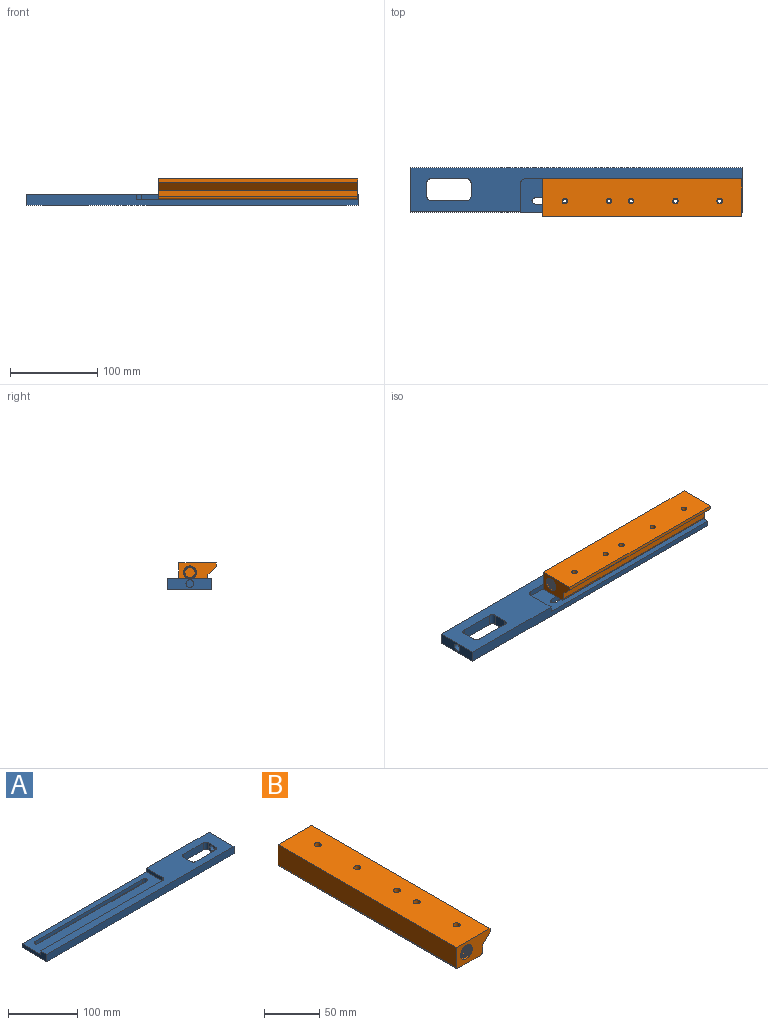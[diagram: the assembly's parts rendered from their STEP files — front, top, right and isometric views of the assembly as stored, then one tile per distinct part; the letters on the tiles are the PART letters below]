
ASSEMBLY  parts=2 mates=1
PART A: 25 faces, bbox 381x50.8x12.7 mm
  f0: plane 381x50.8mm, normal (0,0,-1), area 16366.6mm2, adj f2,f3,f5,f6,f9,f10,f11,f12
  f1: plane 254x38.1mm, normal (0,0,1), area 7951.8mm2, adj f2,f3,f7,f8,f13,f14,f15,f16
  f2: plane 50.8x12.7mm, normal (-1,0,0), area 403.2mm2, adj f0,f1,f3,f4,f5,f8
  f3: plane 381x12.7mm, normal (0,1,0), area 3225.8mm2, adj f0,f1,f2,f4,f6,f7
  f4: plane 381x50.8mm, normal (0,0,1), area 8414.8mm2, adj f2,f3,f5,f6,f7,f8,f9,f10
  f5: plane 381x12.7mm, normal (0,-1,0), area 4838.7mm2, adj f0,f2,f4,f6
  f6: plane 50.8x12.7mm, normal (1,0,0), area 583.1mm2, adj f0,f3,f4,f5,f24
  f7: plane 33.02x6.35mm, normal (-1,0,0), area 209.7mm2, adj f1,f3,f4,f23
  f8: plane 248.92x6.35mm, normal (0,1,0), area 1580.6mm2, adj f1,f2,f4,f23
  f9: plane 15.24x12.7mm, normal (1,0,0), area 193.5mm2, adj f0,f4,f19,f22
  f10: plane 40.64x12.7mm, normal (0,1,0), area 516.1mm2, adj f0,f4,f19,f20
  f11: plane 15.24x12.7mm, normal (-1,0,0), area 131.5mm2, adj f0,f4,f20,f21,f24
  f12: plane 40.64x12.7mm, normal (0,-1,0), area 516.1mm2, adj f0,f4,f21,f22
  f13: plane 218.44x6.35mm, normal (0,-1,0), area 1387.1mm2, adj f0,f1,f16,f17
  f14: plane 218.44x6.35mm, normal (0,1,0), area 1387.1mm2, adj f0,f1,f15,f18
  f15: cylinder r=5.08mm len=6.35mm, axis (0,0,-1), area 42.5mm2, adj f0,f1,f14,f16
  f16: cylinder r=5.08mm len=6.35mm, axis (0,0,1), area 42.5mm2, adj f0,f1,f13,f15
  f17: cylinder r=5.08mm len=6.35mm, axis (0,0,-1), area 42.5mm2, adj f0,f1,f13,f18
  f18: cylinder r=5.08mm len=6.35mm, axis (0,0,1), area 42.5mm2, adj f0,f1,f14,f17
  f19: cylinder r=5.08mm len=12.7mm, axis (0,0,-1), area 101.3mm2, adj f0,f4,f9,f10
  f20: cylinder r=5.08mm len=12.7mm, axis (0,0,1), area 101.3mm2, adj f0,f4,f10,f11
  f21: cylinder r=5.08mm len=12.7mm, axis (0,0,-1), area 101.3mm2, adj f0,f4,f11,f12
  f22: cylinder r=5.08mm len=12.7mm, axis (0,0,1), area 101.3mm2, adj f0,f4,f9,f12
  f23: cylinder r=5.08mm len=6.35mm, axis (0,0,1), area 50.7mm2, adj f1,f4,f7,f8
  f24: cylinder r=4.45mm len=19.24mm, axis (1,0,0), area 537.4mm2, adj f6,f11
PART B: 129 faces, bbox 42.9x228.9x23.9 mm
  f0: cylinder r=3.17mm len=13.02mm, axis (0,0,1), area 235.9mm2, adj f1,f87,f125,f126,f128
  f1: cylinder r=3.17mm len=6.35mm, axis (0,0,1), area 3.2mm2, adj f0,f2,f126,f128
  f2: cylinder r=3.17mm len=6.35mm, axis (0,0,1), area 3.2mm2, adj f1,f3,f126,f128
  f3: cylinder r=3.17mm len=6.35mm, axis (0,0,1), area 3.2mm2, adj f2,f4,f126,f128
  f4: cylinder r=3.17mm len=6.35mm, axis (0,0,1), area 3.2mm2, adj f3,f5,f126,f128
  f5: cylinder r=3.17mm len=6.35mm, axis (0,0,1), area 3.2mm2, adj f4,f6,f126,f128
  f6: cylinder r=3.17mm len=6.35mm, axis (0,0,1), area 3.2mm2, adj f5,f7,f126,f128
  f7: cylinder r=3.17mm len=6.35mm, axis (0,0,1), area 3.2mm2, adj f6,f8,f126,f128
  f8: cylinder r=3.17mm len=6.35mm, axis (0,0,1), area 3.2mm2, adj f7,f9,f126,f128
  f9: cylinder r=3.17mm len=6.01mm, axis (0,0,1), area 1.1mm2, adj f8,f10,f126,f128
  f10: cone r=3.43mm half-angle=45deg, axis (0,0,-1), area 18mm2, adj f9,f80,f126,f127,f128
  f11: cone r=3.43mm half-angle=45deg, axis (0,0,-1), area 18mm2, adj f21,f80,f122,f123,f124
  f12: cylinder r=3.17mm len=13.02mm, axis (0,0,1), area 235.9mm2, adj f13,f87,f121,f122,f124
  f13: cylinder r=3.17mm len=6.35mm, axis (0,0,1), area 3.2mm2, adj f12,f14,f122,f124
  f14: cylinder r=3.17mm len=6.35mm, axis (0,0,1), area 3.2mm2, adj f13,f15,f122,f124
  f15: cylinder r=3.17mm len=6.35mm, axis (0,0,1), area 3.2mm2, adj f14,f16,f122,f124
  f16: cylinder r=3.17mm len=6.35mm, axis (0,0,1), area 3.2mm2, adj f15,f17,f122,f124
  f17: cylinder r=3.17mm len=6.35mm, axis (0,0,1), area 3.2mm2, adj f16,f18,f122,f124
  f18: cylinder r=3.17mm len=6.35mm, axis (0,0,1), area 3.2mm2, adj f17,f19,f122,f124
  f19: cylinder r=3.17mm len=6.35mm, axis (0,0,1), area 3.2mm2, adj f18,f20,f122,f124
  f20: cylinder r=3.17mm len=6.35mm, axis (0,0,1), area 3.2mm2, adj f19,f21,f122,f124
  f21: cylinder r=3.17mm len=6.01mm, axis (0,0,1), area 1.1mm2, adj f11,f20,f122,f124
  f22: cone r=3.43mm half-angle=45deg, axis (0,0,-1), area 17.9mm2, adj f70,f71,f72,f73,f80
  f23: cone r=3.43mm half-angle=45deg, axis (0,0,-1), area 17.9mm2, adj f60,f74,f75,f76,f80
  f24: cone r=3.43mm half-angle=45deg, axis (0,0,-1), area 17.9mm2, adj f50,f77,f78,f79,f80
  f25: cone r=7.18mm half-angle=1.8deg, axis (0,0,-1), area 68mm2, adj f27,f28,f114,f116,f117
  f26: cylinder r=6.86mm len=13.72mm, axis (0,0,-1), area 220.4mm2, adj f27,f111,f112,f113,f116
  f27: cylinder r=6.86mm len=13.72mm, axis (0,0,-1), area 6.7mm2, adj f25,f26,f114,f116
  f28: cone r=7.56mm half-angle=45deg, axis (0,0,-1), area 51.4mm2, adj f25,f80,f115,f116,f117
  f29: cone r=6.86mm half-angle=1.8deg, axis (0,1,0), area 60.7mm2, adj f30,f31,f108,f110
  f30: cylinder r=6.86mm len=13.72mm, axis (0,1,0), area 226.7mm2, adj f29,f104,f105,f106,f107,f110
  f31: cone r=7.56mm half-angle=45deg, axis (0,1,0), area 52.8mm2, adj f29,f32,f81,f108,f109,f110
  f32: cone r=7.56mm half-angle=45deg, axis (0,1,0), area 0.6mm2, adj f31,f108,f109
  f33: cone r=7.18mm half-angle=1.8deg, axis (0,0,-1), area 68mm2, adj f35,f36,f100,f102,f103
  f34: cylinder r=6.86mm len=13.72mm, axis (0,0,-1), area 220.4mm2, adj f35,f97,f98,f99,f102
  f35: cylinder r=6.86mm len=13.72mm, axis (0,0,-1), area 6.7mm2, adj f33,f34,f100,f102
  f36: cone r=7.56mm half-angle=45deg, axis (0,0,-1), area 51.4mm2, adj f33,f80,f101,f102,f103
  f37: cone r=6.86mm half-angle=1.8deg, axis (0,-1,0), area 60.7mm2, adj f38,f39,f94,f96
  f38: cylinder r=6.86mm len=13.72mm, axis (0,-1,0), area 226.7mm2, adj f37,f90,f91,f92,f93,f94,f96
  f39: cone r=7.56mm half-angle=45deg, axis (0,-1,0), area 52.8mm2, adj f37,f40,f82,f94,f95,f96
  f40: cone r=7.56mm half-angle=45deg, axis (0,-1,0), area 0.6mm2, adj f39,f94,f95
  f41: cylinder r=3.17mm len=13.02mm, axis (0,0,1), area 235.9mm2, adj f49,f77,f79,f87,f118
  f42: cylinder r=3.17mm len=6.35mm, axis (0,0,1), area 3.2mm2, adj f43,f50,f77,f79
  f43: cylinder r=3.17mm len=6.35mm, axis (0,0,1), area 3.2mm2, adj f42,f44,f77,f79
  f44: cylinder r=3.17mm len=6.35mm, axis (0,0,1), area 3.2mm2, adj f43,f45,f77,f79
  f45: cylinder r=3.17mm len=6.35mm, axis (0,0,1), area 3.2mm2, adj f44,f46,f77,f79
  f46: cylinder r=3.17mm len=6.35mm, axis (0,0,1), area 3.2mm2, adj f45,f47,f77,f79
  f47: cylinder r=3.17mm len=6.35mm, axis (0,0,1), area 3.2mm2, adj f46,f48,f77,f79
  f48: cylinder r=3.17mm len=6.35mm, axis (0,0,1), area 3.2mm2, adj f47,f49,f77,f79
  f49: cylinder r=3.17mm len=6.35mm, axis (0,0,1), area 3.2mm2, adj f41,f48,f77,f79
  f50: cylinder r=3.17mm len=6.01mm, axis (0,0,1), area 1.1mm2, adj f24,f42,f77,f79
  f51: cylinder r=3.17mm len=13.02mm, axis (0,0,1), area 235.9mm2, adj f59,f74,f76,f87,f119
  f52: cylinder r=3.17mm len=6.35mm, axis (0,0,1), area 3.2mm2, adj f53,f60,f74,f76
  f53: cylinder r=3.17mm len=6.35mm, axis (0,0,1), area 3.2mm2, adj f52,f54,f74,f76
  f54: cylinder r=3.17mm len=6.35mm, axis (0,0,1), area 3.2mm2, adj f53,f55,f74,f76
  f55: cylinder r=3.17mm len=6.35mm, axis (0,0,1), area 3.2mm2, adj f54,f56,f74,f76
  f56: cylinder r=3.17mm len=6.35mm, axis (0,0,1), area 3.2mm2, adj f55,f57,f74,f76
  f57: cylinder r=3.17mm len=6.35mm, axis (0,0,1), area 3.2mm2, adj f56,f58,f74,f76
  f58: cylinder r=3.17mm len=6.35mm, axis (0,0,1), area 3.2mm2, adj f57,f59,f74,f76
  f59: cylinder r=3.17mm len=6.35mm, axis (0,0,1), area 3.2mm2, adj f51,f58,f74,f76
  f60: cylinder r=3.17mm len=6.01mm, axis (0,0,1), area 1.1mm2, adj f23,f52,f74,f76
  f61: cylinder r=3.17mm len=13.02mm, axis (0,0,1), area 235.9mm2, adj f69,f71,f73,f87,f120
  f62: cylinder r=3.17mm len=6.35mm, axis (0,0,1), area 3.2mm2, adj f63,f70,f71,f73
  f63: cylinder r=3.17mm len=6.35mm, axis (0,0,1), area 3.2mm2, adj f62,f64,f71,f73
  f64: cylinder r=3.17mm len=6.35mm, axis (0,0,1), area 3.2mm2, adj f63,f65,f71,f73
  f65: cylinder r=3.17mm len=6.35mm, axis (0,0,1), area 3.2mm2, adj f64,f66,f71,f73
  f66: cylinder r=3.17mm len=6.35mm, axis (0,0,1), area 3.2mm2, adj f65,f67,f71,f73
  f67: cylinder r=3.17mm len=6.35mm, axis (0,0,1), area 3.2mm2, adj f66,f68,f71,f73
  f68: cylinder r=3.17mm len=6.35mm, axis (0,0,1), area 3.2mm2, adj f67,f69,f71,f73
  f69: cylinder r=3.17mm len=6.35mm, axis (0,0,1), area 3.2mm2, adj f61,f68,f71,f73
  f70: cylinder r=3.17mm len=6.01mm, axis (0,0,1), area 1.1mm2, adj f22,f62,f71,f73
  f71: bspline ~11.91x6.35mm, area 145.7mm2, adj f22,f61,f62,f63,f64,f65,f66,f67
  f72: cylinder r=2.35mm len=11.15mm, axis (0,0,-1), area 21.2mm2, adj f22,f71,f73,f120
  f73: bspline ~12.54x6.35mm, area 153.4mm2, adj f22,f61,f62,f63,f64,f65,f66,f67
  f74: bspline ~11.91x6.35mm, area 145.7mm2, adj f23,f51,f52,f53,f54,f55,f56,f57
  f75: cylinder r=2.35mm len=11.15mm, axis (0,0,-1), area 21.2mm2, adj f23,f74,f76,f119
  f76: bspline ~12.7x6.35mm, area 153.4mm2, adj f23,f51,f52,f53,f54,f55,f56,f57
  f77: bspline ~11.91x6.35mm, area 145.7mm2, adj f24,f41,f42,f43,f44,f45,f46,f47
  f78: cylinder r=2.35mm len=11.15mm, axis (0,0,-1), area 21.2mm2, adj f24,f77,f79,f118
  f79: bspline ~12.54x6.35mm, area 153.4mm2, adj f24,f41,f42,f43,f44,f45,f46,f47
  f80: plane 228.6x28.58mm, normal (0,0,-1), area 5988.8mm2, adj f10,f11,f22,f23,f24,f28,f36,f81
  f81: plane 42.86x23.81mm, normal (0,1,0), area 694.9mm2, adj f31,f80,f83,f84,f85,f86,f87,f88
  f82: plane 42.86x23.81mm, normal (0,-1,0), area 694.9mm2, adj f39,f80,f83,f84,f85,f86,f87,f88
  f83: cylinder r=3.17mm len=228.6mm, axis (0,1,0), area 1140.1mm2, adj f80,f81,f82,f84
  f84: plane 228.6x7.15mm, normal (1,0,0), area 1634.5mm2, adj f81,f82,f83,f85
  f85: plane 228.6x9.53mm, normal (0.71,0,-0.71), area 3079.3mm2, adj f81,f82,f84,f86
  f86: plane 228.6x3.96mm, normal (1,0,0), area 905.8mm2, adj f81,f82,f85,f87
  f87: plane 228.6x42.86mm, normal (0,0,1), area 9640mm2, adj f0,f12,f41,f51,f61,f81,f82,f86
  f88: plane 228.6x22.23mm, normal (-1,0,0), area 5080.6mm2, adj f81,f82,f87,f89
  f89: cylinder r=1.59mm len=228.6mm, axis (0,1,0), area 570mm2, adj f80,f81,f82,f88
  f90: plane 13.72x13.72mm, normal (0,-1,0), area 147.8mm2, adj f38
  f91: bspline ~13.76x7.79mm, area 2.7mm2, adj f38,f92,f96
  f92: plane 1.25x0.94mm, normal (-1,0,0), area 0.7mm2, adj f38,f91,f93,f94,f95,f96
  f93: bspline ~13.76x7.79mm, area 0.3mm2, adj f38,f92,f94
  f94: bspline ~14.33x14.31mm, area 318.3mm2, adj f37,f38,f39,f40,f92,f93,f95
  f95: bspline ~12.6x12.58mm, area 48.6mm2, adj f39,f40,f92,f94,f96
  f96: bspline ~14.42x14.37mm, area 327.6mm2, adj f37,f38,f39,f91,f92,f95
  f97: plane 13.72x13.72mm, normal (0,0,-1), area 147.8mm2, adj f34
  f98: bspline ~13.79x9.41mm, area 0.3mm2, adj f34,f99,f102
  f99: plane 1.25x0.94mm, normal (-1,0,0), area 0.7mm2, adj f34,f98,f100,f101,f102,f103
  f100: bspline ~13.79x10.17mm, area 3.1mm2, adj f33,f35,f99,f103
  f101: bspline ~12.33x12.29mm, area 49.1mm2, adj f36,f99,f102,f103
  f102: bspline ~14.6x14.58mm, area 307mm2, adj f33,f34,f35,f36,f98,f99,f101
  f103: bspline ~14.53x14.42mm, area 313.5mm2, adj f33,f36,f99,f100,f101
  f104: plane 13.72x13.72mm, normal (0,1,0), area 147.8mm2, adj f30
  f105: bspline ~13.76x7.79mm, area 2.7mm2, adj f30,f107,f110
  f106: bspline ~13.76x7.79mm, area 0.3mm2, adj f30,f107,f108
  f107: plane 1.25x0.94mm, normal (-1,0,0), area 0.7mm2, adj f30,f105,f106,f108,f109,f110
  f108: bspline ~14.35x14.33mm, area 318.3mm2, adj f29,f31,f32,f106,f107,f109
  f109: bspline ~12.6x12.58mm, area 48.6mm2, adj f31,f32,f107,f108,f110
  f110: bspline ~14.42x14.37mm, area 327.5mm2, adj f29,f30,f31,f105,f107,f109
  f111: plane 13.72x13.72mm, normal (0,0,-1), area 147.8mm2, adj f26
  f112: bspline ~13.79x9.41mm, area 0.3mm2, adj f26,f113,f116
  f113: plane 1.25x0.94mm, normal (-1,0,0), area 0.7mm2, adj f26,f112,f114,f115,f116,f117
  f114: bspline ~13.79x10.17mm, area 3.1mm2, adj f25,f27,f113,f117
  f115: bspline ~12.33x12.29mm, area 49.1mm2, adj f28,f113,f116,f117
  f116: bspline ~14.6x14.58mm, area 295.4mm2, adj f25,f26,f27,f28,f112,f113,f115
  f117: bspline ~14.53x14.42mm, area 313.5mm2, adj f25,f28,f113,f114,f115
  f118: plane 1.11x0.83mm, normal (1,0,0), area 0.5mm2, adj f41,f77,f78,f79
  f119: plane 1.11x0.83mm, normal (1,0,0), area 0.5mm2, adj f51,f74,f75,f76
  f120: plane 1.11x0.83mm, normal (1,0,0), area 0.5mm2, adj f61,f71,f72,f73
  f121: plane 1.11x0.83mm, normal (1,0,0), area 0.5mm2, adj f12,f122,f123,f124
  f122: bspline ~12.7x6.35mm, area 153.4mm2, adj f11,f12,f13,f14,f15,f16,f17,f18
  f123: cylinder r=2.35mm len=11.15mm, axis (0,0,1), area 21.2mm2, adj f11,f121,f122,f124
  f124: bspline ~11.91x6.35mm, area 145.7mm2, adj f11,f12,f13,f14,f15,f16,f17,f18
  f125: plane 1.11x0.83mm, normal (1,0,0), area 0.5mm2, adj f0,f126,f127,f128
  f126: bspline ~12.54x6.35mm, area 153.4mm2, adj f0,f1,f2,f3,f4,f5,f6,f7
  f127: cylinder r=2.35mm len=11.15mm, axis (0,0,1), area 21.2mm2, adj f10,f125,f126,f128
  f128: bspline ~11.91x6.35mm, area 145.7mm2, adj f0,f1,f2,f3,f4,f5,f6,f7
PLACE A rot(axis=(0,0,-1),180deg) t=(-312.65,-53.14,-64.64)mm
PLACE B rot(axis=(0,0,-1),90deg) t=(-253.32,7.33,-58.29)mm
MATE planar A.f1 <-> B.f80  axis (0,0,1) through (-156.61,1.79,-58.29)mm
